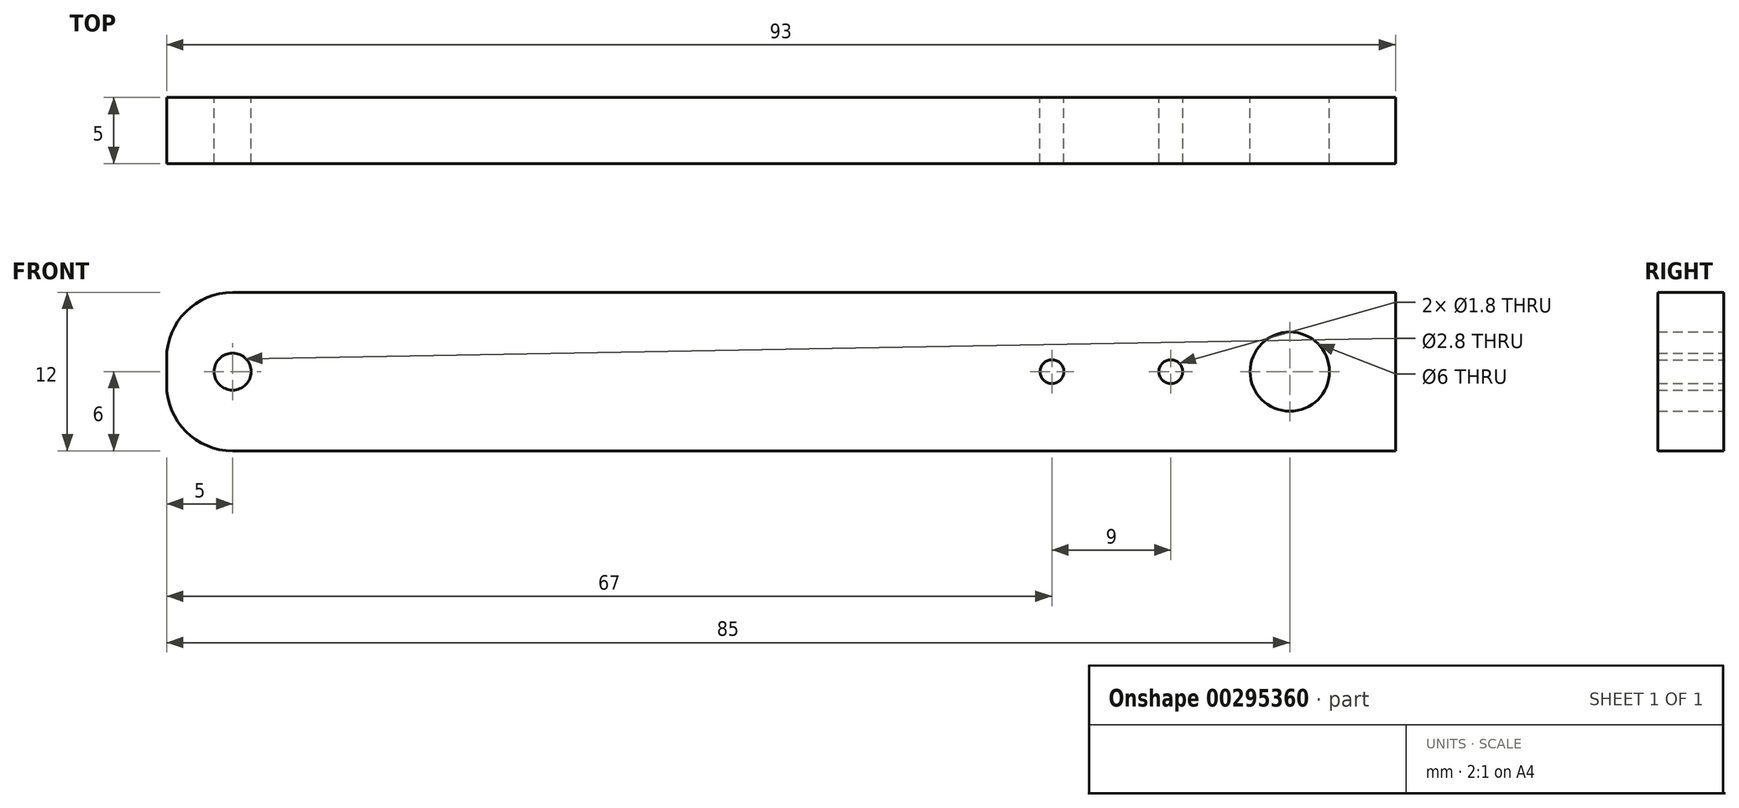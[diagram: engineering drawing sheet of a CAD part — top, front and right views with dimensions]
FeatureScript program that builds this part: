
annotation { "Feature Type Name" : "Feature", "Feature Type Description" : "" }
export const myFeature = defineFeature(function(context is Context, id is Id, definition is map)
    precondition{}
    {
        {
            var Q0;
            Q0=qCreatedBy(makeId("Front.planeOp"),FACE);
            var sketch = newSketch(context, id + "F0", { "sketchPlane" : qUnion([Q0])});
            skCircle(sketch, "E0", {"center": v(-80, 0) * mm, "radius": 1.4 * mm});
            skLineSegment(sketch, "E1.bottom", {"start": v(-11, -6) * mm, "end": v(-80, -6) * mm});
            skLineSegment(sketch, "E1.top", {"start": v(-11, 6) * mm, "end": v(-80, 6) * mm});
            skLineSegment(sketch, "E1.right", {"start": v(-85, -1) * mm, "end": v(-85, 1) * mm});
            skCircle(sketch, "E2", {"center": v(-9, 0) * mm, "radius": 0.9 * mm});
            skCircle(sketch, "E3", {"center": v(-18, 0) * mm, "radius": 0.9 * mm});
            skPoint(sketch, "E4", {"position": v(-2, 0) * mm});
            skPoint(sketch, "E5", {"position": v(8, 0) * mm});
            skPoint(sketch, "E6.visualSharp", {"position": v(-85, 6) * mm});
            skArc(sketch, "E6.filletArc", {"start": v(-80, 6) * mm, "mid": v(-83.54, 4.54) * mm, "end": v(-85, 1) * mm});
            skPoint(sketch, "E7.visualSharp", {"position": v(-85, -6) * mm});
            skArc(sketch, "E7.filletArc", {"start": v(-85, -1) * mm, "mid": v(-83.54, -4.54) * mm, "end": v(-80, -6) * mm});
            skCircle(sketch, "E8", {"center": v(0, 0) * mm, "radius": 3 * mm});
            skLineSegment(sketch, "E9", {"start": v(8, 6) * mm, "end": v(8, -6) * mm});
            skLineSegment(sketch, "E10", {"start": v(8, -6) * mm, "end": v(-11, -6) * mm});
            skLineSegment(sketch, "E11", {"start": v(-11, 6) * mm, "end": v(8, 6) * mm});
            skSolve(sketch);
        }
        {
            var Q0;
            Q0=makeQuery(id+"F0.imprint","IMPRINT",FACE,{"disambiguationData":[TD([[makeQuery(id+"F0.imprint","IMPRINT",EDGE,{"derivedFrom":sQuery(id+"F0.wireOp",EDGE,"E0")}),-1.0]])]});
            extrude(context, id + "F1", {"entities" : qUnion([Q0]), "depth" : 5 * mm});
        }
    });
